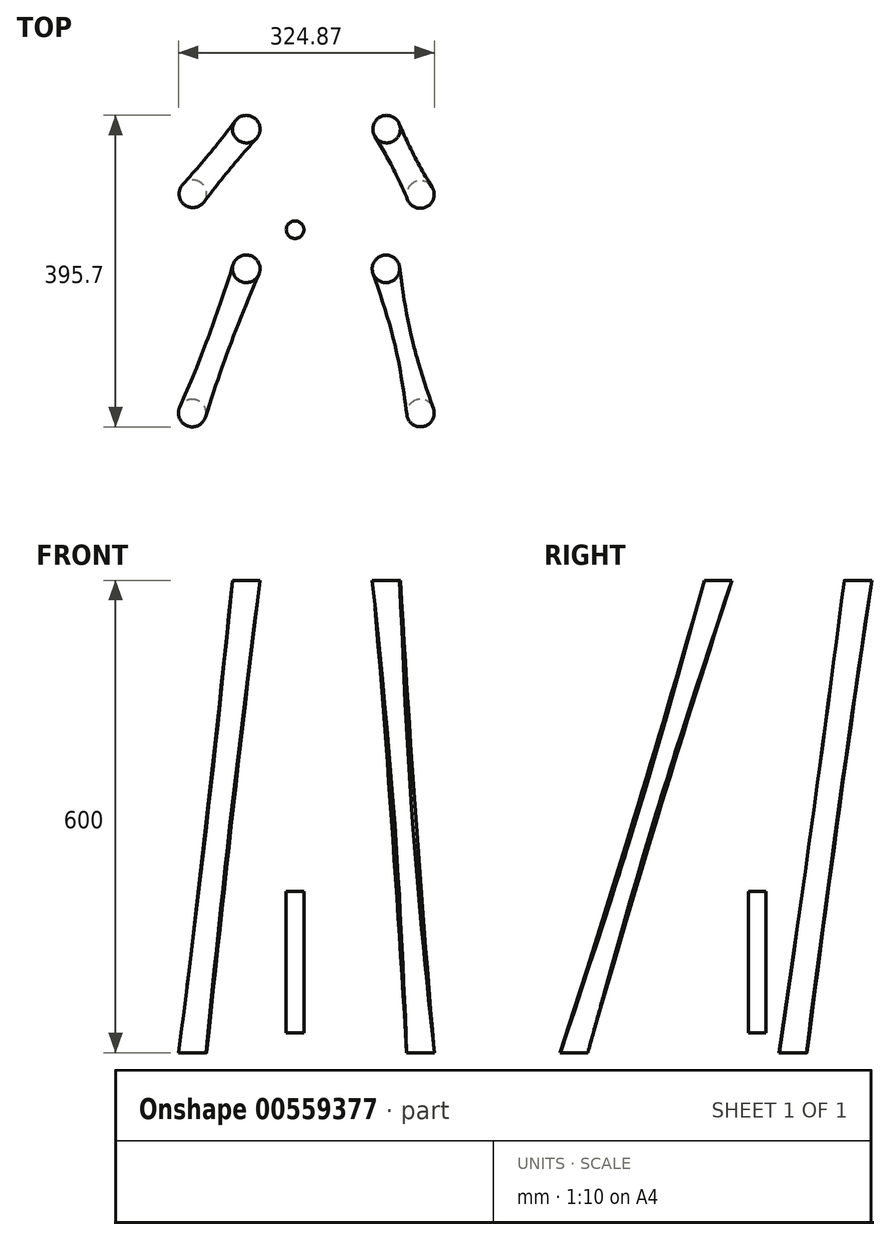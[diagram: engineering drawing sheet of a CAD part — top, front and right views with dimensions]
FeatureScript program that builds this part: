
annotation { "Feature Type Name" : "Feature", "Feature Type Description" : "" }
export const myFeature = defineFeature(function(context is Context, id is Id, definition is map)
    precondition{}
    {
        {
            var Q0;
            Q0=qCreatedBy(makeId("Top.planeOp"),FACE);
            cPlane(context, id + "F0", {"entities" : qUnion([Q0]), "cplaneType" : CPlaneType.OFFSET, "offset" : 25 * mm, "width" : 150 * mm, "height" : 150 * mm});
        }
        {
            var Q0;
            Q0=qCreatedBy(makeId("Top.planeOp"),FACE);
            cPlane(context, id + "F1", {"entities" : qUnion([Q0]), "cplaneType" : CPlaneType.OFFSET, "offset" : 0 * mm, "width" : 150 * mm, "height" : 150 * mm});
        }
        {
            var Q0;
            Q0=qCreatedBy(id+"F1.planeOp",FACE);
            var sketch = newSketch(context, id + "F2", { "sketchPlane" : qUnion([Q0])});
            skCircle(sketch, "E0", {"center": v(-154.1, 71.45) * mm, "radius": 17.5 * mm});
            skCircle(sketch, "E1", {"center": v(-154.88, -207.1) * mm, "radius": 17.5 * mm});
            skCircle(sketch, "E2", {"center": v(135, -206.97) * mm, "radius": 17.5 * mm});
            skCircle(sketch, "E3", {"center": v(134.92, 70.58) * mm, "radius": 17.5 * mm});
            skSolve(sketch);
        }
        {
            var Q0;
            Q0=qCreatedBy(makeId("Top.planeOp"),FACE);
            cPlane(context, id + "F3", {"entities" : qUnion([Q0]), "cplaneType" : CPlaneType.OFFSET, "offset" : 600 * mm, "width" : 150 * mm, "height" : 150 * mm});
        }
        {
            var Q0;
            Q0=qCreatedBy(id+"F3.planeOp",FACE);
            var sketch = newSketch(context, id + "F4", { "sketchPlane" : qUnion([Q0])});
            skCircle(sketch, "E4", {"center": v(-86.29, 153.6) * mm, "radius": 17.5 * mm});
            skCircle(sketch, "E5", {"center": v(91.92, 153.6) * mm, "radius": 17.5 * mm});
            skCircle(sketch, "E6", {"center": v(91.14, -23.82) * mm, "radius": 17.5 * mm});
            skCircle(sketch, "E7", {"center": v(-86.29, -23.82) * mm, "radius": 17.5 * mm});
            skSolve(sketch);
        }
        {
            var Q0;
            Q0=makeQuery(id+"F2.imprint","IMPRINT",FACE,{"disambiguationData":[TD([[makeQuery(id+"F2.imprint","IMPRINT",EDGE,{"derivedFrom":sQuery(id+"F2.wireOp",EDGE,"E3")}),1.0]])]});
            var Q1;
            Q1=makeQuery(id+"F4.imprint","IMPRINT",FACE,{"disambiguationData":[TD([[makeQuery(id+"F4.imprint","IMPRINT",EDGE,{"derivedFrom":sQuery(id+"F4.wireOp",EDGE,"E5")}),1.0]])]});
            loft(context, id + "F5", {"sheetProfilesArray" : [{ "sheetProfileEntities" : qUnion([Q0]) }, { "sheetProfileEntities" : qUnion([Q1]) }]});
        }
        {
            var Q0;
            Q0=makeQuery(id+"F4.imprint","IMPRINT",FACE,{"disambiguationData":[TD([[makeQuery(id+"F4.imprint","IMPRINT",EDGE,{"derivedFrom":sQuery(id+"F4.wireOp",EDGE,"E6")}),1.0]])]});
            var Q1;
            Q1=makeQuery(id+"F2.imprint","IMPRINT",FACE,{"disambiguationData":[TD([[makeQuery(id+"F2.imprint","IMPRINT",EDGE,{"derivedFrom":sQuery(id+"F2.wireOp",EDGE,"E2")}),1.0]])]});
            loft(context, id + "F6", {"sheetProfilesArray" : [{ "sheetProfileEntities" : qUnion([Q0]) }, { "sheetProfileEntities" : qUnion([Q1]) }]});
        }
        {
            var Q0;
            Q0=makeQuery(id+"F4.imprint","IMPRINT",FACE,{"disambiguationData":[TD([[makeQuery(id+"F4.imprint","IMPRINT",EDGE,{"derivedFrom":sQuery(id+"F4.wireOp",EDGE,"E7")}),1.0]])]});
            var Q1;
            Q1=makeQuery(id+"F2.imprint","IMPRINT",FACE,{"disambiguationData":[TD([[makeQuery(id+"F2.imprint","IMPRINT",EDGE,{"derivedFrom":sQuery(id+"F2.wireOp",EDGE,"E1")}),1.0]])]});
            loft(context, id + "F7", {"sheetProfilesArray" : [{ "sheetProfileEntities" : qUnion([Q0]) }, { "sheetProfileEntities" : qUnion([Q1]) }]});
        }
        {
            var Q0;
            Q0=makeQuery(id+"F4.imprint","IMPRINT",FACE,{"disambiguationData":[TD([[makeQuery(id+"F4.imprint","IMPRINT",EDGE,{"derivedFrom":sQuery(id+"F4.wireOp",EDGE,"E4")}),1.0]])]});
            var Q1;
            Q1=makeQuery(id+"F2.imprint","IMPRINT",FACE,{"disambiguationData":[TD([[makeQuery(id+"F2.imprint","IMPRINT",EDGE,{"derivedFrom":sQuery(id+"F2.wireOp",EDGE,"E0")}),1.0]])]});
            loft(context, id + "F8", {"sheetProfilesArray" : [{ "sheetProfileEntities" : qUnion([Q0]) }, { "sheetProfileEntities" : qUnion([Q1]) }]});
        }
        {
            var Q0;
            Q0=qCreatedBy(id+"F0.planeOp",FACE);
            var sketch = newSketch(context, id + "F9", { "sketchPlane" : qUnion([Q0])});
            skCircle(sketch, "E8", {"center": v(-24.33, 25.9) * mm, "radius": 11.16 * mm});
            skSolve(sketch);
        }
        {
            var Q0;
            Q0 = qSketchRegion(id + "F9", true);
            extrude(context, id + "F10", {"entities" : qUnion([Q0]), "operationType" : NewBodyOperationType.ADD, "depth" : 180 * mm, "offsetDistance" : 25 * mm});
        }
    });
